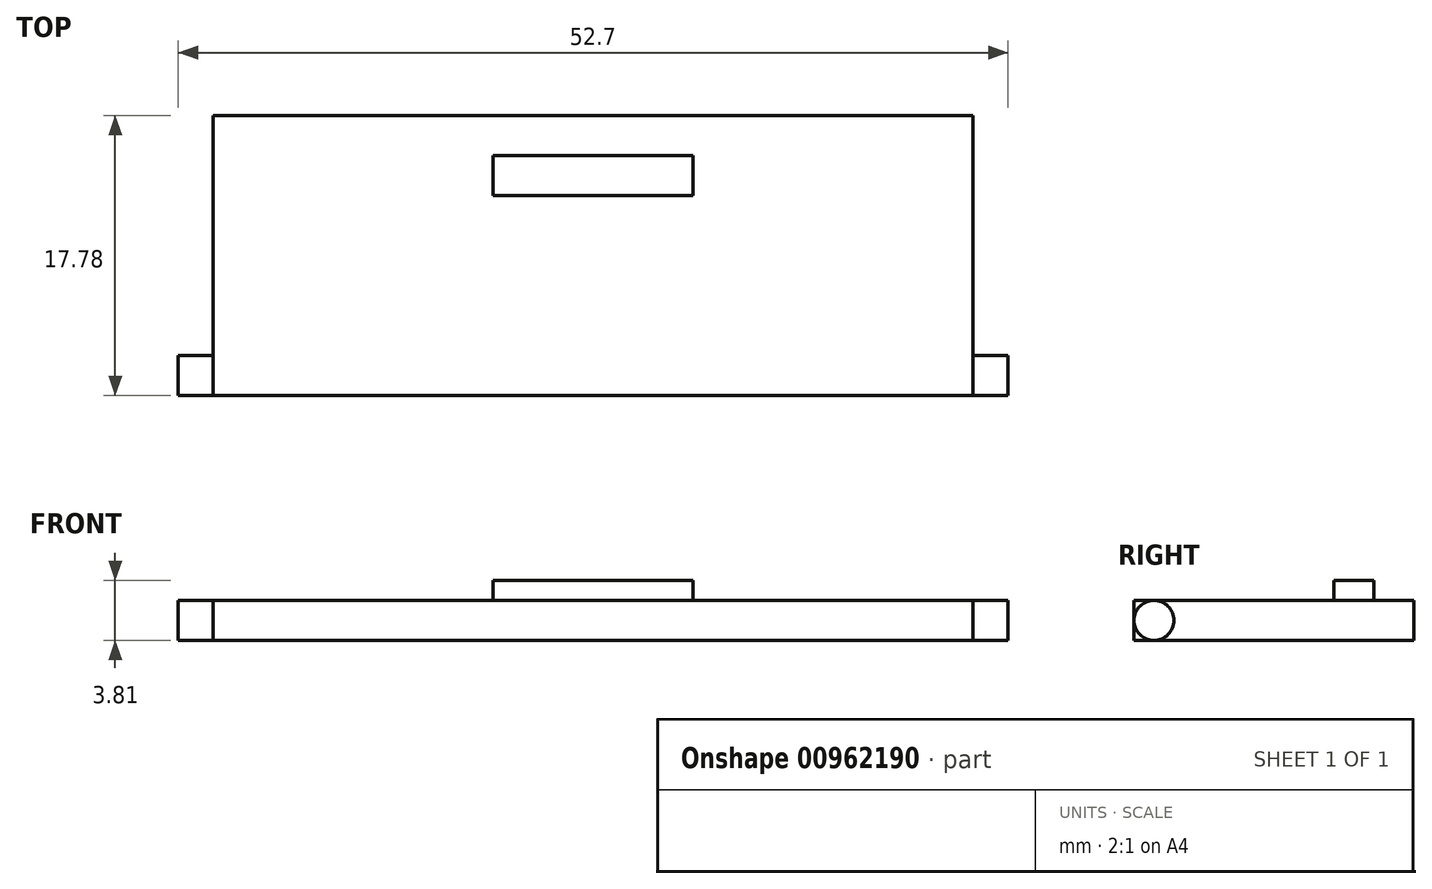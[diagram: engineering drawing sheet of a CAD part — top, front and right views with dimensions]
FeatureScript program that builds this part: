
annotation { "Feature Type Name" : "Feature", "Feature Type Description" : "" }
export const myFeature = defineFeature(function(context is Context, id is Id, definition is map)
    precondition{}
    {
        {
            var Q0;
            Q0=qCreatedBy(makeId("Top.planeOp"),FACE);
            var sketch = newSketch(context, id + "F0", { "sketchPlane" : qUnion([Q0])});
            skLineSegment(sketch, "E0.bottom", {"start": v(24.13, 8.9) * mm, "end": v(-24.13, 8.9) * mm});
            skLineSegment(sketch, "E0.top", {"start": v(24.13, -8.89) * mm, "end": v(-24.13, -8.89) * mm});
            skLineSegment(sketch, "E0.left", {"start": v(24.13, 8.9) * mm, "end": v(24.13, -8.89) * mm});
            skLineSegment(sketch, "E0.right", {"start": v(-24.13, 8.9) * mm, "end": v(-24.13, -8.89) * mm});
            skPoint(sketch, "E0.middle", {"position": v(0, 0) * mm});
            skSolve(sketch);
        }
        {
            var Q0;
            Q0=makeQuery(id+"F0.imprint","IMPRINT",FACE,{"disambiguationData":[TD([[makeQuery(id+"F0.imprint","IMPRINT",EDGE,{"derivedFrom":sQuery(id+"F0.wireOp",EDGE,"E0.bottom")}),1.0]])]});
            extrude(context, id + "F1", {"entities" : qUnion([Q0]), "depth" : 2.54 * mm, "offsetDistance" : 25.4 * mm});
        }
        {
            var Q0;
            Q0=qCreatedBy(makeId("Right.planeOp"),FACE);
            var sketch = newSketch(context, id + "F2", { "sketchPlane" : qUnion([Q0])});
            skCircle(sketch, "E1", {"center": v(-7.62, 1.27) * mm, "radius": 1.27 * mm});
            skSolve(sketch);
        }
        {
            var Q0;
            Q0 = qSketchRegion(id + "F2", true);
            extrude(context, id + "F3", {"entities" : qUnion([Q0]), "operationType" : NewBodyOperationType.ADD, "endBound" : BoundingType.SYMMETRIC, "depth" : 52.7 * mm, "offsetDistance" : 25.4 * mm});
        }
        {
            var Q0;
            Q0=makeQuery(id+"F1.opExtrude","CAP_FACE",FACE,{"disambiguationData":[OSD([sQuery(id+"F0.wireOp",EDGE,"E0.bottom"),sQuery(id+"F0.wireOp",EDGE,"E0.top"),sQuery(id+"F0.wireOp",EDGE,"E0.left"),sQuery(id+"F0.wireOp",EDGE,"E0.right")])],"isStart":false});
            var sketch = newSketch(context, id + "F4", { "sketchPlane" : qUnion([Q0])});
            skLineSegment(sketch, "E2.bottom", {"start": v(6.35, 6.35) * mm, "end": v(-6.35, 6.35) * mm});
            skLineSegment(sketch, "E2.top", {"start": v(6.35, 3.81) * mm, "end": v(-6.35, 3.81) * mm});
            skLineSegment(sketch, "E2.left", {"start": v(6.35, 6.35) * mm, "end": v(6.35, 3.81) * mm});
            skLineSegment(sketch, "E2.right", {"start": v(-6.35, 6.35) * mm, "end": v(-6.35, 3.81) * mm});
            skPoint(sketch, "E2.middle", {"position": v(0, 5.08) * mm});
            skSolve(sketch);
        }
        {
            var Q0;
            Q0=makeQuery(id+"F4.imprint","IMPRINT",FACE,{"disambiguationData":[TD([[makeQuery(id+"F4.imprint","IMPRINT",EDGE,{"derivedFrom":sQuery(id+"F4.wireOp",EDGE,"E2.bottom")}),1.0]])]});
            extrude(context, id + "F5", {"entities" : qUnion([Q0]), "operationType" : NewBodyOperationType.ADD, "depth" : 1.27 * mm, "offsetDistance" : 25.4 * mm});
        }
    });
